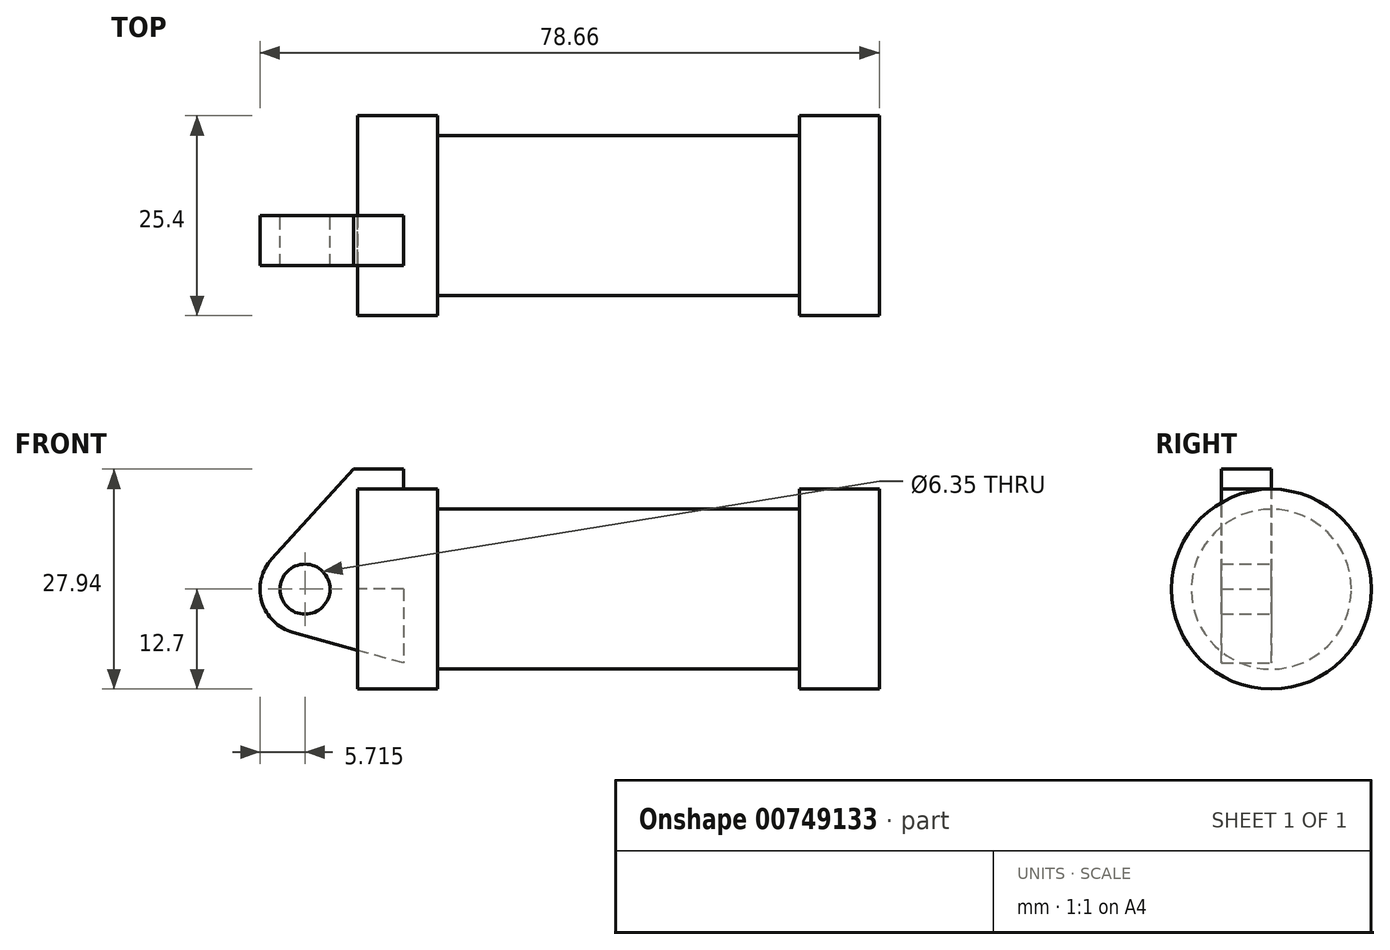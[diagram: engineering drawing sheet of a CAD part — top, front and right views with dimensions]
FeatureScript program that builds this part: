
annotation { "Feature Type Name" : "Feature", "Feature Type Description" : "" }
export const myFeature = defineFeature(function(context is Context, id is Id, definition is map)
    precondition{}
    {
        {
            var Q0;
            Q0=qCreatedBy(makeId("Front.planeOp"),FACE);
            var sketch = newSketch(context, id + "F0", { "sketchPlane" : qUnion([Q0])});
            skLineSegment(sketch, "E0", {"start": v(0, 0) * mm, "end": v(0, 12.7) * mm});
            skLineSegment(sketch, "E1", {"start": v(0, 12.7) * mm, "end": v(10.16, 12.7) * mm});
            skLineSegment(sketch, "E2", {"start": v(10.16, 12.7) * mm, "end": v(10.16, 10.16) * mm});
            skLineSegment(sketch, "E3", {"start": v(10.16, 10.16) * mm, "end": v(56.13, 10.16) * mm});
            skLineSegment(sketch, "E4", {"start": v(56.13, 10.16) * mm, "end": v(56.13, 12.7) * mm});
            skLineSegment(sketch, "E5", {"start": v(56.13, 12.7) * mm, "end": v(66.3, 12.7) * mm});
            skLineSegment(sketch, "E6", {"start": v(66.3, 12.7) * mm, "end": v(66.3, 0) * mm});
            skLineSegment(sketch, "E7", {"start": v(66.3, 0) * mm, "end": v(0, 0) * mm});
            skLineSegment(sketch, "E8", {"start": v(5.84, 15.24) * mm, "end": v(-0.5, 15.24) * mm});
            skLineSegment(sketch, "E9", {"start": v(-0.5, 15.24) * mm, "end": v(-10.88, 3.85) * mm});
            skLineSegment(sketch, "E10", {"start": v(0, 0) * mm, "end": v(-6.65, 0) * mm});
            skCircle(sketch, "E11", {"center": v(-6.65, 0) * mm, "radius": 5.72 * mm});
            skCircle(sketch, "E12", {"center": v(-6.65, 0) * mm, "radius": 3.18 * mm});
            skLineSegment(sketch, "E13", {"start": v(5.84, 15.24) * mm, "end": v(5.84, -9.4) * mm});
            skLineSegment(sketch, "E14", {"start": v(5.84, -9.4) * mm, "end": v(-8.18, -5.5) * mm});
            skSolve(sketch);
        }
        {
            var Q0;
            {var subQ0=sQuery(id+"F0.wireOp",EDGE,"E0");Q0=makeQuery(id+"F0.imprint","IMPRINT",FACE,{"disambiguationData":[TD([[makeQuery(id+"F0.imprint","IMPRINT",EDGE,{"derivedFrom":subQ0}),-1.0]])]});}
            var Q1;
            {var subQ0=sQuery(id+"F0.wireOp",EDGE,"E2");Q1=makeQuery(id+"F0.imprint","IMPRINT",FACE,{"disambiguationData":[TD([[makeQuery(id+"F0.imprint","IMPRINT",EDGE,{"derivedFrom":subQ0}),-1.0]])]});}
            var Q2;
            Q2=sQuery(id+"F0.wireOp",EDGE,"E7");
            revolve(context, id + "F1", {"surfaceOperationType" : NewSurfaceOperationType.NEW, "entities" : qUnion([Q0, Q1]), "axis" : qUnion([Q2]), "revolveType" : RevolveType.FULL});
        }
        {
            var Q0;
            {var subQ1=sQuery(id+"F0.wireOp",EDGE,"E0");Q0=makeQuery(id+"F0.imprint","IMPRINT",FACE,{"disambiguationData":[TD([[makeQuery(id+"F0.imprint","IMPRINT",EDGE,{"derivedFrom":subQ1}),1.0]])]});}
            var Q1;
            {var subQ5=sQuery(id+"F0.wireOp",EDGE,"E12");Q1=makeQuery(id+"F0.imprint","IMPRINT",FACE,{"disambiguationData":[TD([[makeQuery(id+"F0.imprint","IMPRINT",EDGE,{"derivedFrom":subQ5}),-1.0]])]});}
            var Q2;
            {var subQ0=sQuery(id+"F0.wireOp",EDGE,"E14");Q2=makeQuery(id+"F0.imprint","IMPRINT",FACE,{"disambiguationData":[TD([[makeQuery(id+"F0.imprint","IMPRINT",EDGE,{"derivedFrom":subQ0}),-1.0]])]});}
            extrude(context, id + "F2", {"entities" : qUnion([Q0, Q1, Q2]), "depth" : 6.35 * mm, "offsetDistance" : 25.4 * mm});
        }
    });
